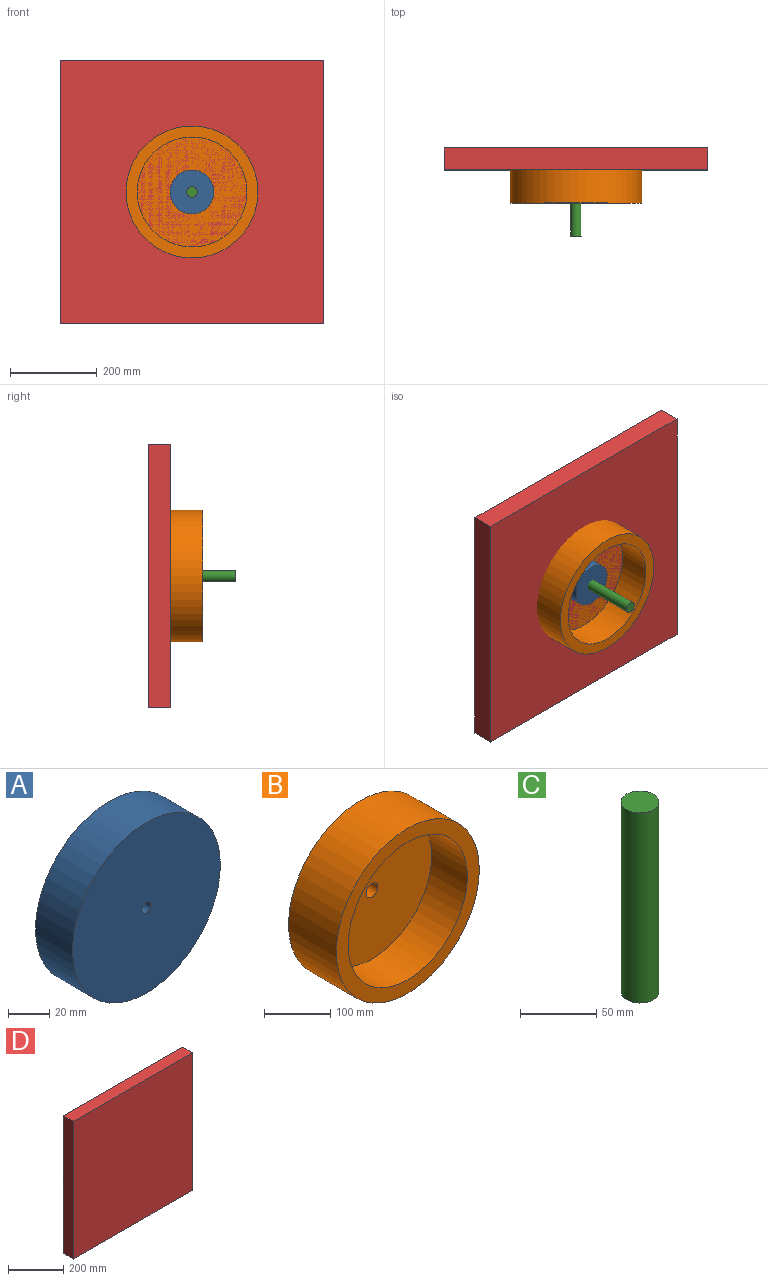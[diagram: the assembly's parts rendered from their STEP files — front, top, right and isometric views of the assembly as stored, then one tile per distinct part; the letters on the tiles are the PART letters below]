
ASSEMBLY  parts=4 mates=3
PART A: 4 faces, bbox 101.6x25.4x101.6 mm
  f0: cylinder r=3.17mm len=25.4mm, axis (0,1,0), area 506.7mm2, adj f2,f3
  f1: cylinder r=50.8mm len=101.6mm, axis (0,1,0), area 8107.3mm2, adj f2,f3
  f2: plane 101.6x101.6mm, normal (0,-1,0), area 8075.7mm2, adj f0,f1
  f3: plane 101.6x101.6mm, normal (0,1,0), area 8075.7mm2, adj f0,f1
PART B: 6 faces, bbox 304.8x101.6x304.8 mm
  f0: cylinder r=12.7mm len=25.4mm, axis (0,1,0), area 2026.8mm2, adj f1,f2
  f1: plane 254x254mm, normal (0,-1,0), area 50164mm2, adj f0,f3
  f2: plane 304.8x304.8mm, normal (0,1,0), area 72459.2mm2, adj f0,f4
  f3: cylinder r=127mm len=254mm, axis (0,1,0), area 60804.9mm2, adj f1,f5
  f4: cylinder r=152.4mm len=304.8mm, axis (0,1,0), area 97287.8mm2, adj f2,f5
  f5: plane 304.8x304.8mm, normal (0,-1,0), area 22295.1mm2, adj f3,f4
PART C: 3 faces, bbox 24.9x24.9x152.4 mm
  f0: plane 24.89x24.89mm, normal (0,0,1), area 486.6mm2, adj f2
  f1: plane 24.89x24.89mm, normal (0,0,-1), area 486.6mm2, adj f2
  f2: cylinder r=12.45mm len=152.4mm, axis (0,0,-1), area 11917.8mm2, adj f0,f1
PART D: 6 faces, bbox 609.6x50.8x609.6 mm
  f0: plane 609.6x50.8mm, normal (0,0,-1), area 30967.7mm2, adj f1,f3,f4,f5
  f1: plane 609.6x50.8mm, normal (1,0,0), area 30967.7mm2, adj f0,f2,f4,f5
  f2: plane 609.6x50.8mm, normal (0,0,1), area 30967.7mm2, adj f1,f3,f4,f5
  f3: plane 609.6x50.8mm, normal (-1,0,0), area 30967.7mm2, adj f0,f2,f4,f5
  f4: plane 609.6x609.6mm, normal (0,-1,0), area 371612.2mm2, adj f0,f1,f2,f3
  f5: plane 609.6x609.6mm, normal (0,1,0), area 371612.2mm2, adj f0,f1,f2,f3
PLACE A t=(-226.02,179.64,541.39)mm
PLACE B rot(axis=(0,-1,0),95.3deg) t=(-226.02,205.04,541.39)mm
PLACE C rot(axis=(-1,0,0),90deg) t=(-268.95,-8.31,541.39)mm
PLACE D t=(-226.02,230.44,541.39)mm fixed
MATE revolute B.f0 <-> C.f2  axis (0,-1,0) through (-226.02,179.64,541.39)mm
MATE fastened C.f2 <-> D.f4  axis (0,-1,0) through (-226.02,179.64,541.39)mm
MATE revolute A.f0 <-> C.f2  axis (0,1,0) through (-226.02,179.64,541.39)mm
